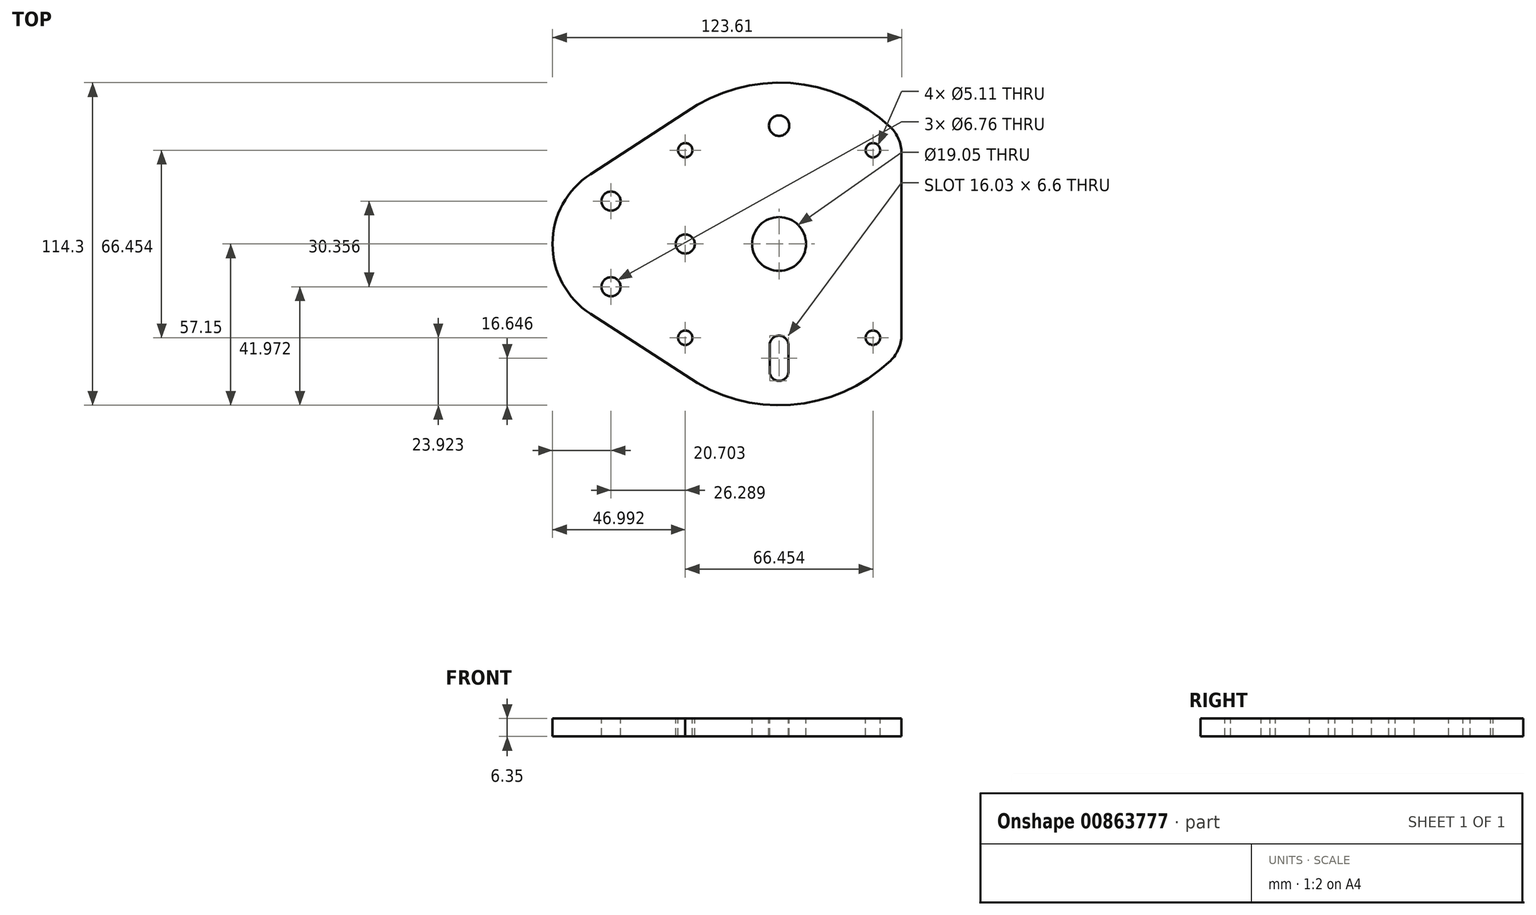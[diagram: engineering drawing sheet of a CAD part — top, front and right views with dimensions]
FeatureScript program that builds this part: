
annotation { "Feature Type Name" : "Feature", "Feature Type Description" : "" }
export const myFeature = defineFeature(function(context is Context, id is Id, definition is map)
    precondition{}
    {
        {
            var Q0;
            Q0=qCreatedBy(makeId("Top.planeOp"),FACE);
            var sketch = newSketch(context, id + "F0", { "sketchPlane" : qUnion([Q0])});
            skLineSegment(sketch, "E0", {"start": v(0, 0) * mm, "end": v(-58.93, 0) * mm, "construction": true});
            skPoint(sketch, "E1", {"position": v(-29.46, 0) * mm});
            skCircle(sketch, "E2", {"center": v(-29.46, 0) * mm, "radius": 17.53 * mm, "construction": true});
            skPoint(sketch, "E3", {"position": v(21.29, 0) * mm});
            skPoint(sketch, "E4", {"position": v(-11.94, 0) * mm});
            skCircle(sketch, "E5", {"center": v(21.29, 0) * mm, "radius": 19.05 * mm, "construction": true});
            skCircle(sketch, "E6", {"center": v(21.29, 0) * mm, "radius": 31.75 * mm, "construction": true});
            skCircle(sketch, "E7", {"center": v(54.52, 33.23) * mm, "radius": 2.55 * mm});
            skCircle(sketch, "E8", {"center": v(21.29, 0) * mm, "radius": 9.53 * mm});
            skCircle(sketch, "E9", {"center": v(21.29, 0) * mm, "radius": 35.94 * mm, "construction": true});
            skLineSegment(sketch, "E10", {"start": v(21.29, 57.15) * mm, "end": v(21.29, -57.15) * mm, "construction": true});
            skCircle(sketch, "E11", {"center": v(21.29, 0) * mm, "radius": 45.34 * mm, "construction": true});
            skLineSegment(sketch, "E12", {"start": v(21.29, 0) * mm, "end": v(61.7, 40.41) * mm, "construction": true});
            skCircle(sketch, "E13", {"center": v(21.29, 0) * mm, "radius": 46.99 * mm, "construction": true});
            skCircle(sketch, "E14.1.0", {"center": v(-11.94, 33.23) * mm, "radius": 2.55 * mm});
            skCircle(sketch, "E14.2.0", {"center": v(-11.94, -33.23) * mm, "radius": 2.55 * mm});
            skCircle(sketch, "E14.3.0", {"center": v(54.52, -33.23) * mm, "radius": 2.55 * mm});
            skLineSegment(sketch, "E15", {"start": v(21.29, 0) * mm, "end": v(-19.12, 40.41) * mm, "construction": true});
            skLineSegment(sketch, "E16", {"start": v(21.29, 0) * mm, "end": v(-19.12, -40.41) * mm, "construction": true});
            skCircle(sketch, "E17", {"center": v(21.29, 0) * mm, "radius": 57.15 * mm, "construction": true});
            skCircle(sketch, "E18.converted", {"center": v(-29.46, 0) * mm, "radius": 29.46 * mm, "construction": true});
            skPoint(sketch, "E19", {"position": v(78.44, 0) * mm});
            skLineSegment(sketch, "E20", {"start": v(-38.23, 28.13) * mm, "end": v(-38.23, -28.13) * mm, "construction": true});
            skLineSegment(sketch, "E21", {"start": v(-11.94, -46.5) * mm, "end": v(-11.94, 46.5) * mm, "construction": true});
            skLineSegment(sketch, "E22", {"start": v(17.99, -35.79) * mm, "end": v(17.99, -45.22) * mm});
            skLineSegment(sketch, "E23", {"start": v(24.6, -35.79) * mm, "end": v(24.6, -45.22) * mm});
            skArc(sketch, "E24", {"start": v(17.99, -35.79) * mm, "mid": v(21.29, -32.49) * mm, "end": v(24.6, -35.79) * mm});
            skArc(sketch, "E25", {"start": v(17.99, -45.22) * mm, "mid": v(21.29, -48.52) * mm, "end": v(24.6, -45.22) * mm});
            skLineSegment(sketch, "E26", {"start": v(64.68, 32.16) * mm, "end": v(64.68, -18.05) * mm});
            skArc(sketch, "E27", {"start": v(60.74, 41.35) * mm, "mid": v(25.33, 57) * mm, "end": v(-11.94, 46.5) * mm});
            skArc(sketch, "E28", {"start": v(-11.94, -46.5) * mm, "mid": v(25.33, -57) * mm, "end": v(60.74, -41.35) * mm});
            skPoint(sketch, "E29.visualSharp", {"position": v(64.68, 37.2) * mm});
            skArc(sketch, "E29.filletArc", {"start": v(64.68, 32.16) * mm, "mid": v(63.65, 37.15) * mm, "end": v(60.74, 41.35) * mm});
            skPoint(sketch, "E30.visualSharp", {"position": v(64.68, -37.2) * mm});
            skArc(sketch, "E30.filletArc", {"start": v(60.74, -41.35) * mm, "mid": v(63.65, -37.15) * mm, "end": v(64.68, -32.16) * mm});
            skPoint(sketch, "E31.visualSharp", {"position": v(-38.23, 28.13) * mm});
            skPoint(sketch, "E32.visualSharp", {"position": v(-38.23, -28.13) * mm});
            skLineSegment(sketch, "E33.trimOffspring", {"start": v(64.68, -18.05) * mm, "end": v(64.68, -32.16) * mm});
            skLineSegment(sketch, "E34", {"start": v(-11.94, 46.5) * mm, "end": v(-45.5, 24.72) * mm});
            skLineSegment(sketch, "E35", {"start": v(-11.94, -46.5) * mm, "end": v(-45.5, -24.72) * mm});
            skArc(sketch, "E36", {"start": v(-45.5, 24.72) * mm, "mid": v(-58.93, 0) * mm, "end": v(-45.5, -24.72) * mm});
            skCircle(sketch, "E37", {"center": v(21.29, 41.91) * mm, "radius": 3.62 * mm});
            skPoint(sketch, "E38", {"position": v(-38.23, 15.18) * mm});
            skPoint(sketch, "E39", {"position": v(-38.23, -15.18) * mm});
            skCircle(sketch, "E40", {"center": v(-38.23, 15.18) * mm, "radius": 3.38 * mm});
            skCircle(sketch, "E41", {"center": v(-11.94, 0) * mm, "radius": 3.38 * mm});
            skCircle(sketch, "E42", {"center": v(-38.23, -15.18) * mm, "radius": 3.38 * mm});
            skSolve(sketch);
        }
        {
            var Q0;
            Q0=makeQuery(id+"F0.imprint","IMPRINT",FACE,{"disambiguationData":[TD([[makeQuery(id+"F0.imprint","IMPRINT",EDGE,{"derivedFrom":sQuery(id+"F0.wireOp",EDGE,"E7")}),-1.0]])]});
            extrude(context, id + "F1", {"entities" : qUnion([Q0]), "oppositeDirection" : true, "depth" : 6.35 * mm, "offsetDistance" : 25.4 * mm});
        }
    });
